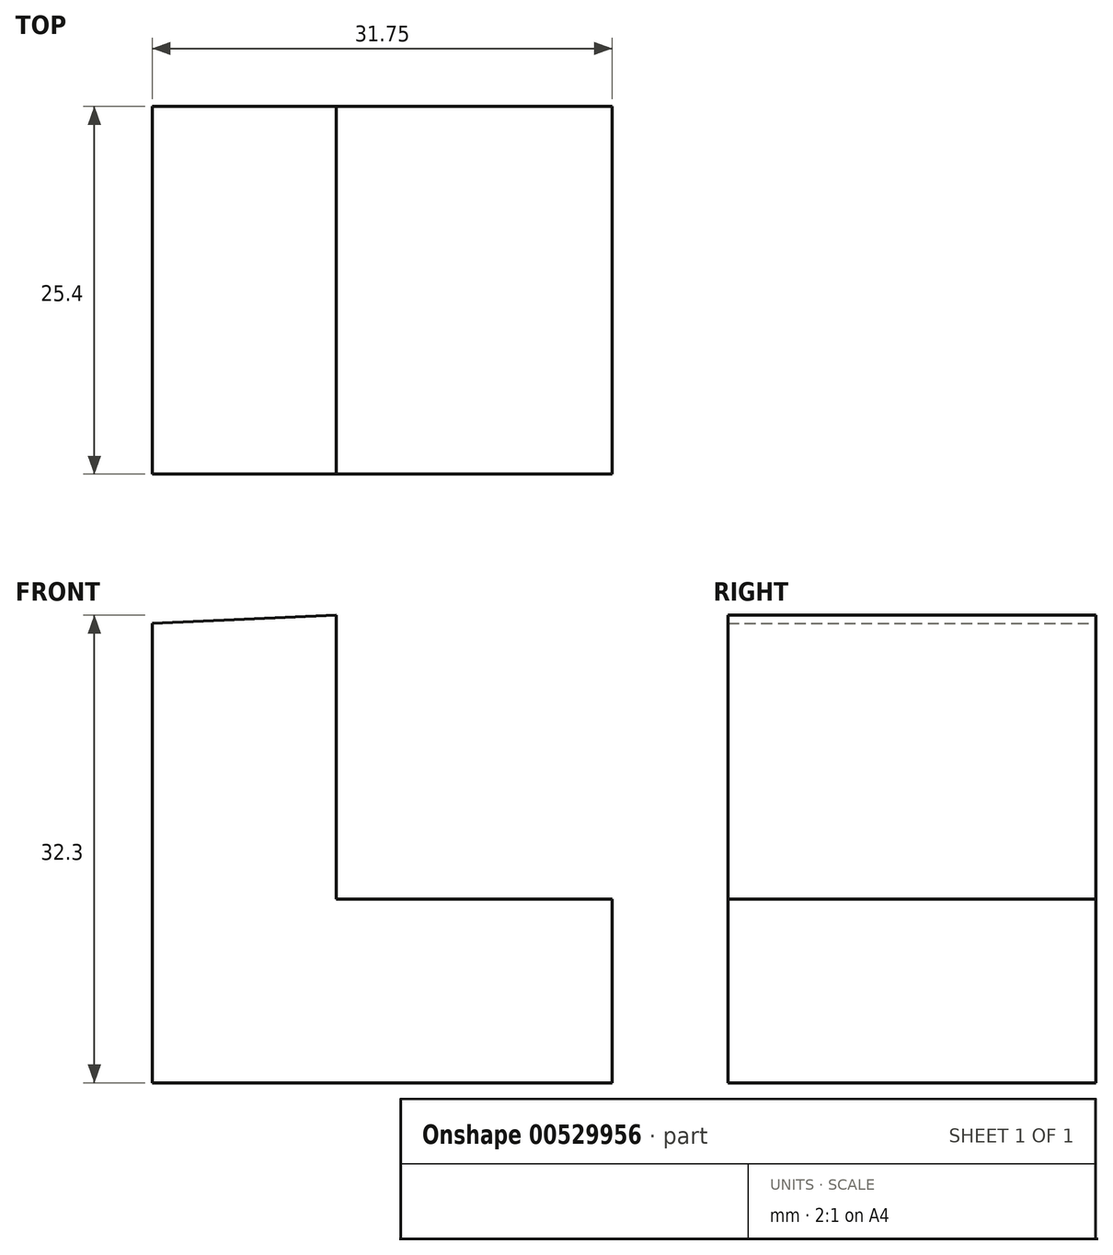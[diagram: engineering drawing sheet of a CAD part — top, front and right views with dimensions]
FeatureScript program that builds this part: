
annotation { "Feature Type Name" : "Feature", "Feature Type Description" : "" }
export const myFeature = defineFeature(function(context is Context, id is Id, definition is map)
    precondition{}
    {
        {
            var Q0;
            Q0=qCreatedBy(makeId("Front.planeOp"),FACE);
            var sketch = newSketch(context, id + "F0", { "sketchPlane" : qUnion([Q0])});
            skLineSegment(sketch, "E0", {"start": v(-67.2, 27.23) * mm, "end": v(-67.2, -4.52) * mm});
            skLineSegment(sketch, "E1", {"start": v(-67.2, -4.52) * mm, "end": v(-35.45, -4.52) * mm});
            skLineSegment(sketch, "E2", {"start": v(-35.45, -4.52) * mm, "end": v(-35.45, 8.18) * mm});
            skLineSegment(sketch, "E3", {"start": v(-35.45, 8.18) * mm, "end": v(-60.85, 8.18) * mm});
            skLineSegment(sketch, "E4", {"start": v(-54.5, 2.38) * mm, "end": v(-54.5, 27.78) * mm});
            skLineSegment(sketch, "E5", {"start": v(-54.5, 27.78) * mm, "end": v(-67.2, 27.23) * mm});
            skSolve(sketch);
        }
        {
            var Q0;
            Q0 = qSketchRegion(id + "F0", true);
            extrude(context, id + "F1", {"entities" : qUnion([Q0]), "depth" : 25.4 * mm, "offsetDistance" : 25.4 * mm});
        }
    });
